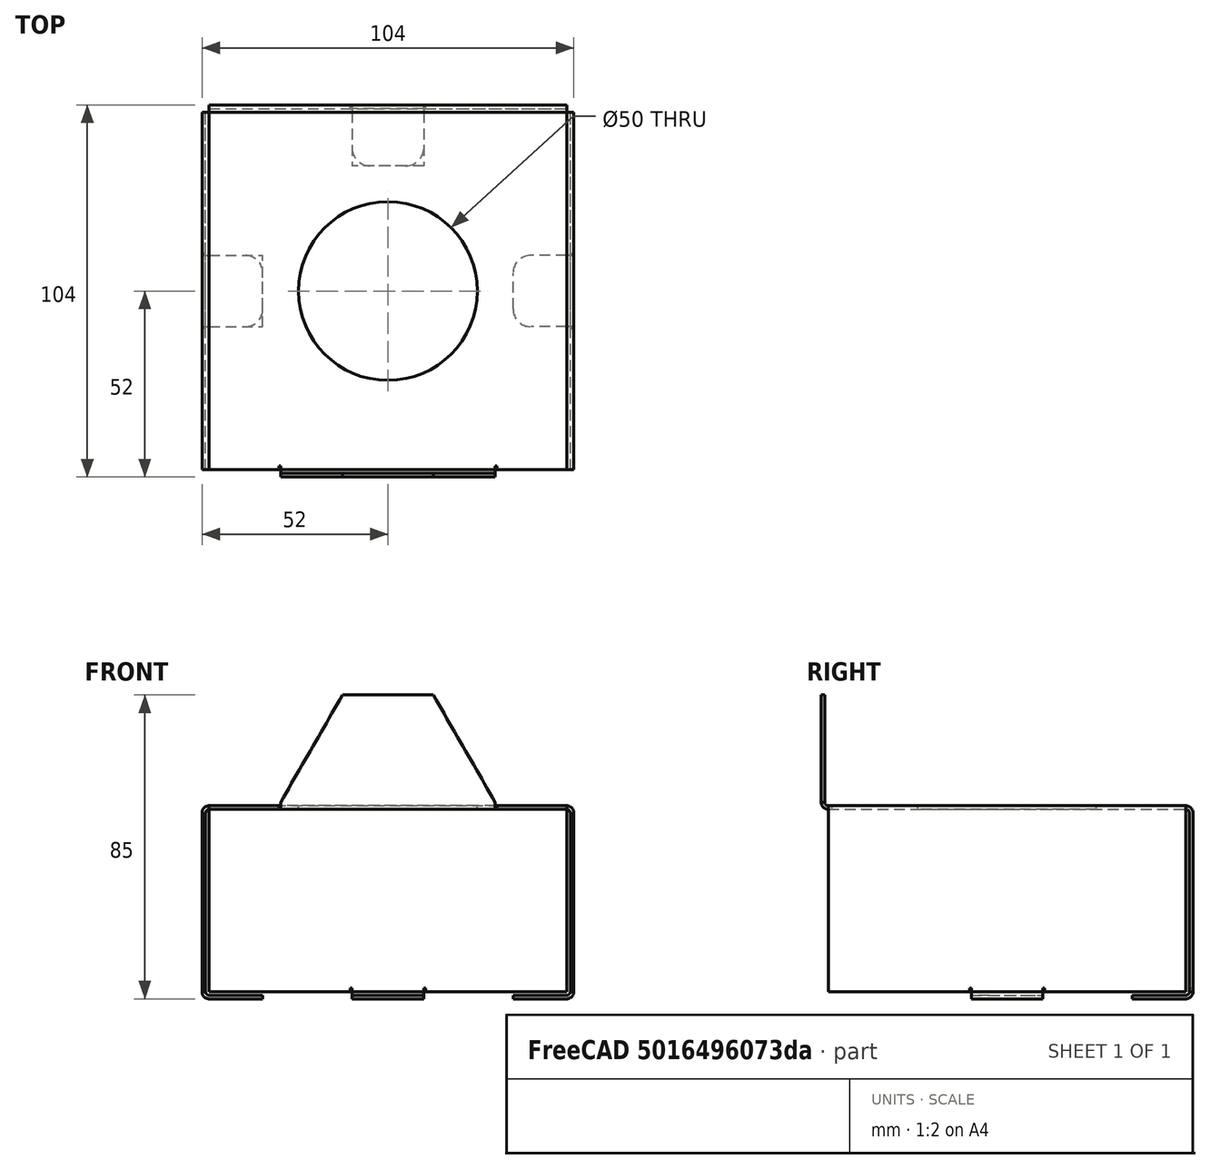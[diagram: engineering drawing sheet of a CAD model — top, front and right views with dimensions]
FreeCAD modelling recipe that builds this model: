
FCSTD DOCUMENT  (FreeCAD 0.17R13247 (Git))
Label: CAIXA
License: All rights reserved
LicenseURL: http://en.wikipedia.org/wiki/All_rights_reserved
objects: Part::FeaturePython×7, Part::Box×1, Part::Fillet×1, Part::Cylinder×1, Part::Cut×1
note: 11 computed .brp shape members not serialized (recipe doc carries the construction recipe); baked Part::Feature solids carry a one-line shape summary decoded from their .brp

FEATURE [Part::Box] Box  label="Cubo"
  AttacherType = Attacher::AttachEngine3D
  Height = 1
  Length = 100
  Width = 100
FEATURE [Part::FeaturePython] Bend  # WARN: FeaturePython — macro-defined, semantics opaque (R4)
  angle = 90
  baseObject = -> Box [Face2]
  gap1 = 0
  gap2 = 0
  invert = true
  length = 50
  miterangle1 = 0
  miterangle2 = 0
  radius = 1
  reliefd = 1
  reliefw = 0.5
FEATURE [Part::FeaturePython] Bend001  # WARN: FeaturePython — macro-defined, semantics opaque (R4)
  angle = 90
  baseObject = -> Bend [Face12]
  gap1 = 0
  gap2 = 0
  invert = true
  length = 50
  miterangle1 = 0
  miterangle2 = 0
  radius = 1
  reliefd = 1
  reliefw = 0.5
FEATURE [Part::FeaturePython] Bend002  # WARN: FeaturePython — macro-defined, semantics opaque (R4)
  angle = 90
  baseObject = -> Bend001 [Face13]
  gap1 = 0
  gap2 = 0
  invert = true
  length = 50
  miterangle1 = 0
  miterangle2 = 0
  radius = 1
  reliefd = 1
  reliefw = 0.5
FEATURE [Part::FeaturePython] Bend003  # WARN: FeaturePython — macro-defined, semantics opaque (R4)
  angle = 90
  baseObject = -> Bend002 [Face1]
  gap1 = 40
  gap2 = 40
  invert = true
  length = 15
  miterangle1 = 0
  miterangle2 = 0
  radius = 1
  reliefd = 1
  reliefw = 0.5
FEATURE [Part::FeaturePython] Bend004  # WARN: FeaturePython — macro-defined, semantics opaque (R4)
  angle = 90
  baseObject = -> Bend003 [Face42]
  gap1 = 40
  gap2 = 40
  invert = true
  length = 15
  miterangle1 = 0
  miterangle2 = 0
  radius = 1
  reliefd = 1
  reliefw = 0.5
FEATURE [Part::FeaturePython] Bend005  # WARN: FeaturePython — macro-defined, semantics opaque (R4)
  angle = 90
  baseObject = -> Bend004 [Face43]
  gap1 = 40
  gap2 = 40
  invert = true
  length = 15
  miterangle1 = 0
  miterangle2 = 0
  radius = 1
  reliefd = 1
  reliefw = 0.5
FEATURE [Part::Fillet] Fillet
  Base = -> Bend005
  Edges = 6 edges r=5: [Edge1,Edge3,Edge177,Edge178,Edge179,Edge180]
FEATURE [Part::FeaturePython] Bend006  # WARN: FeaturePython — macro-defined, semantics opaque (R4)
  angle = 90
  baseObject = -> Fillet [Face33]
  gap1 = 20
  gap2 = 20
  invert = false
  length = 30
  miterangle1 = 30
  miterangle2 = 30
  radius = 1
  reliefd = 1
  reliefw = 0.5
FEATURE [Part::Cylinder] Cylinder  label="Cilindro"
  Angle = 360
  AttacherType = Attacher::AttachEngine3D
  Height = 10
  Placement = pos=(50,50,-5) rot=(0,0,1;0rad)
  Radius = 25
FEATURE [Part::Cut] Cut
  Base = -> Bend006
  Tool = -> Cylinder
